# Revit family: TH1025551_Grifería para Lavamanos Monocontrol Thames Alta
name_source: partatom
category: Plumbing Fixtures
units: mm (PartAtom-declared; Revit-internal decimal feet)

## family parameters
Always vertical = Yes
Cut with Voids When Loaded = No
OmniClass Number = 23.21.21.19
OmniClass Title = Commercial Dishwasher Equipment
Part Type = Normal
Room Calculation Point = No
Round Connector Dimension = Use Diameter
Shared = No
Work Plane-Based = No

## types (1)
- TH1025551_Grifería para Lavamanos Monocontrol Thames Alta
    Acabado = Cromado
    Alto = 25.05 cm
    Altura de la grifería = Alta
    Ancho = 5.2 cm
    Capacidad de flujo = 8.30 l/m máximo a 60 psi
    Colección = Vida 2015
    Consumo de agua = 8.3 lt
    Creado por = IDD
    Description = La línea Thames posee un diseño que combina formas redondas y cuadradas; además, entrega a los ambientes un toque de elegancia y distinción. ¡Adquiérela ahora!
    Fecha de creación = 27/07/2020
    Garantía = 30 años en estructura
    Garantías de otros componentes = 5 años en acabados
    Incluye = Cuerpo, Manija
    Largo = 14.2 cm
    Línea = Thames
    Material = Corona_Cromado
    Materiales = Metalico
    Productos compatibles = Lavamanos tipo vessel
    Rango de presión de agua = Entre 20 y 125 psi
    ResisteResistencia = Resistente a la corrosión pelado y decoloración por agua. Resistente al efecto de jabones y limpiadores de tocador
    Sistema de accionamiento = Palanca
    Tecnologías = DuraCrome
    Temperatura de uso = Entre 5˚C y 71˚C
    Tipo de chorro = Espumoso
    Tipo de grifería = Monocontrol
    Tipo de manija/accionamiento = Palanca
    URL = https://corona.co
    Uso = Residencial

## geometry (parser evidence)
native form markers: Sweep x5
no freeform markers — native parametric forms only
